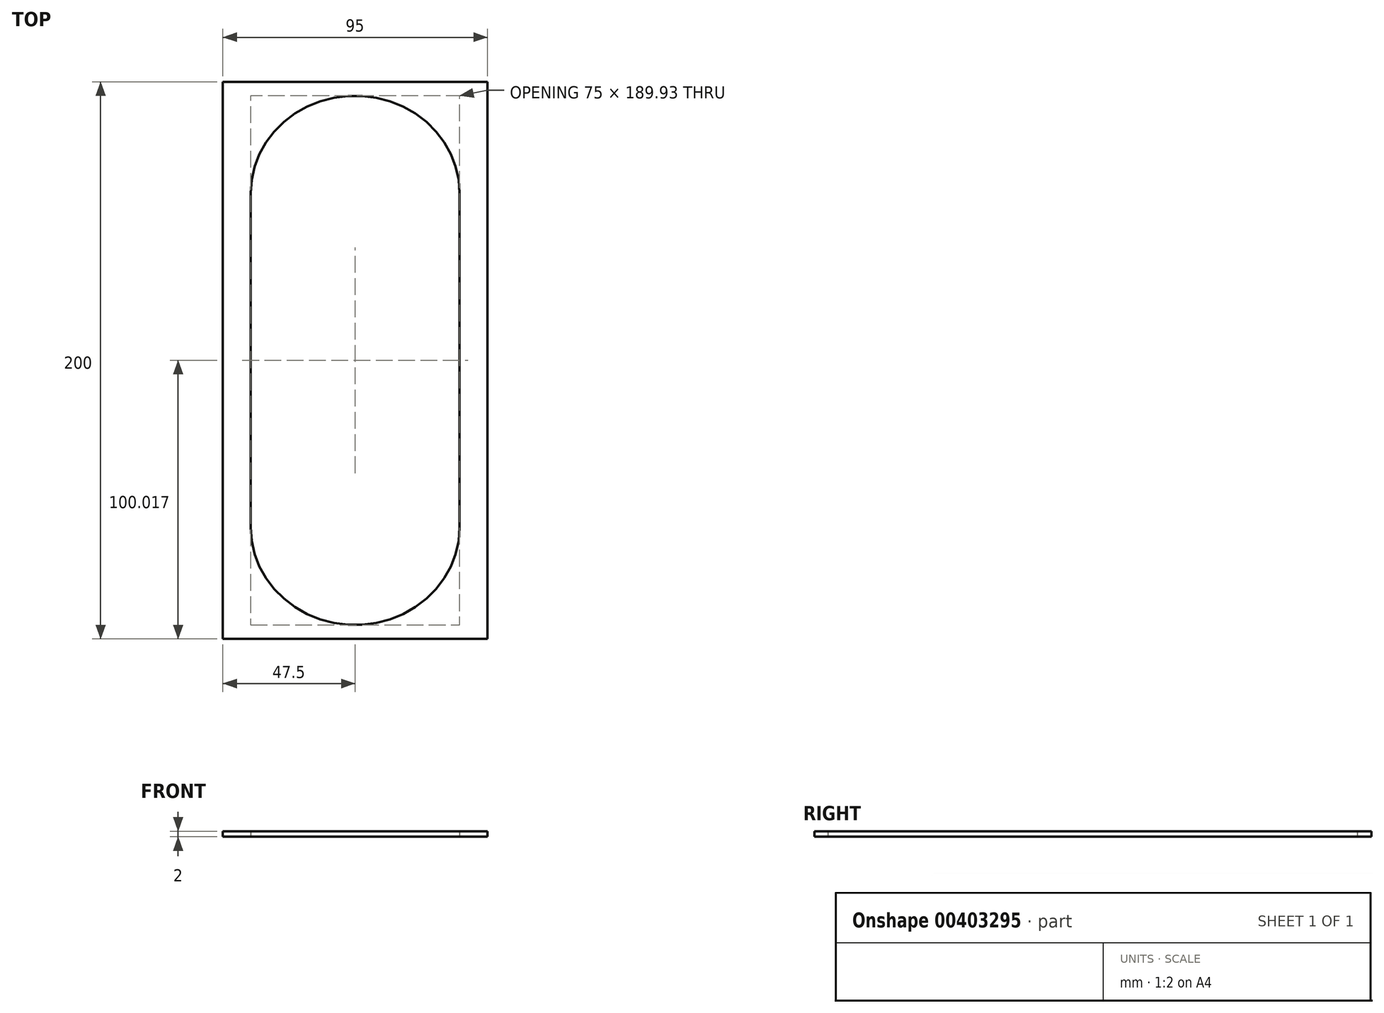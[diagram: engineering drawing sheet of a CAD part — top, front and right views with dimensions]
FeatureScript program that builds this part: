
annotation { "Feature Type Name" : "Feature", "Feature Type Description" : "" }
export const myFeature = defineFeature(function(context is Context, id is Id, definition is map)
    precondition{}
    {
        {
            var Q0;
            Q0=qCreatedBy(makeId("Top.planeOp"),FACE);
            var sketch = newSketch(context, id + "F0", { "sketchPlane" : qUnion([Q0])});
            skLineSegment(sketch, "E0.bottom", {"start": v(-47.5, -100) * mm, "end": v(47.5, -100) * mm});
            skLineSegment(sketch, "E0.top", {"start": v(-47.5, 100) * mm, "end": v(47.5, 100) * mm});
            skLineSegment(sketch, "E0.left", {"start": v(-47.5, -100) * mm, "end": v(-47.5, 100) * mm});
            skLineSegment(sketch, "E0.right", {"start": v(47.5, -100) * mm, "end": v(47.5, 100) * mm});
            skPoint(sketch, "E0.middle", {"position": v(0, 0) * mm});
            skLineSegment(sketch, "E1.bottom", {"start": v(-37.5, -60) * mm, "end": v(37.5, -60) * mm});
            skLineSegment(sketch, "E1.top", {"start": v(-37.5, 60) * mm, "end": v(37.5, 60) * mm});
            skLineSegment(sketch, "E1.left", {"start": v(-37.5, -60) * mm, "end": v(-37.5, 60) * mm});
            skLineSegment(sketch, "E1.right", {"start": v(37.5, -60) * mm, "end": v(37.5, 60) * mm});
            skEllipse(sketch, "E2", {"center": v(0, 60) * mm, "majorRadius": 37.5 * mm, "minorRadius": 34.98 * mm, "majorAxis": v(-1, 0)});
            skEllipse(sketch, "E3", {"center": v(0, -60) * mm, "majorRadius": 37.5 * mm, "minorRadius": 34.95 * mm, "majorAxis": v(-1, 0)});
            skSolve(sketch);
        }
        {
            var Q0;
            Q0=makeQuery(id+"F0.imprint","IMPRINT",FACE,{"disambiguationData":[TD([[makeQuery(id+"F0.imprint","IMPRINT",EDGE,{"derivedFrom":sQuery(id+"F0.wireOp",EDGE,"E0.bottom")}),1.0]])]});
            extrude(context, id + "F1", {"entities" : qUnion([Q0]), "depth" : 2 * mm});
        }
    });
